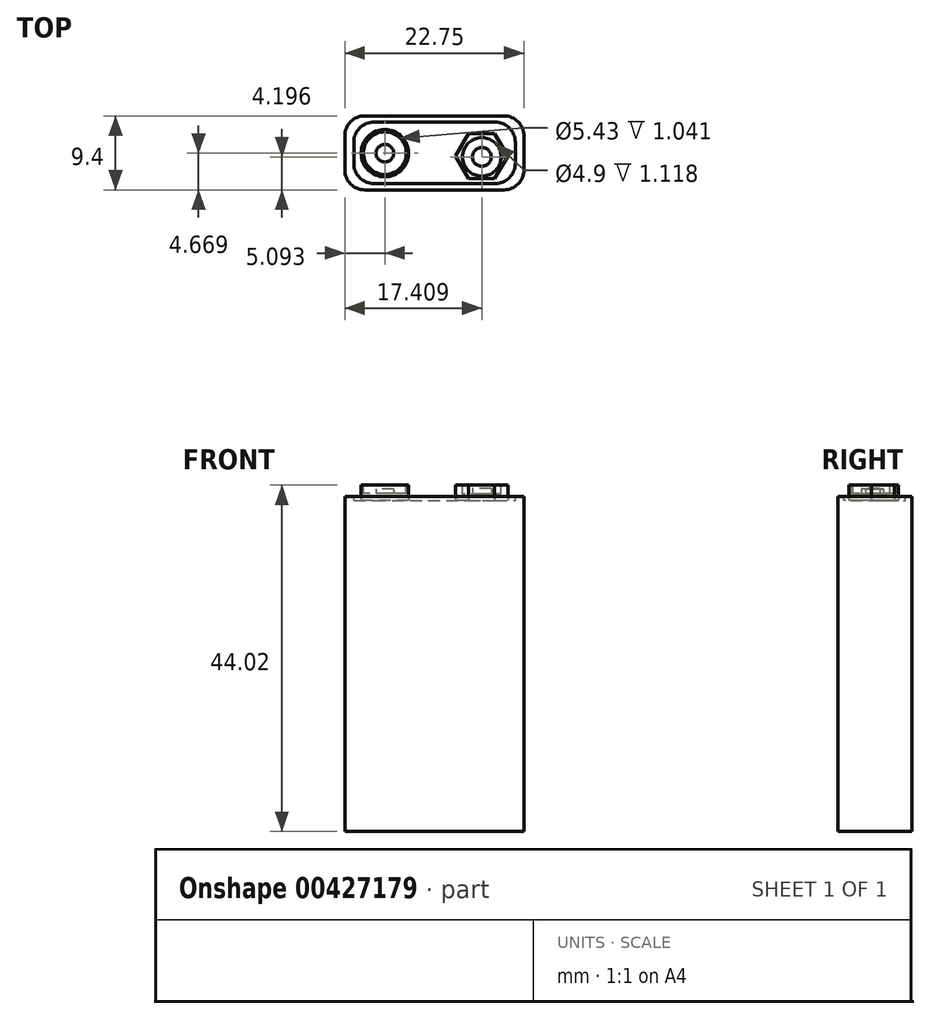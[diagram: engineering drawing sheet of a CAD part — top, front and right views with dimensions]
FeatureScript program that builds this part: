
annotation { "Feature Type Name" : "Feature", "Feature Type Description" : "" }
export const myFeature = defineFeature(function(context is Context, id is Id, definition is map)
    precondition{}
    {
        {
            var Q0;
            Q0=qCreatedBy(makeId("Front.planeOp"),FACE);
            var sketch = newSketch(context, id + "F0", { "sketchPlane" : qUnion([Q0])});
            skLineSegment(sketch, "E0.bottom", {"start": v(-9.62, 20.63) * mm, "end": v(13.13, 20.63) * mm});
            skLineSegment(sketch, "E0.top", {"start": v(-9.62, -21.92) * mm, "end": v(13.13, -21.92) * mm});
            skLineSegment(sketch, "E0.left", {"start": v(-9.62, 20.63) * mm, "end": v(-9.62, -21.92) * mm});
            skLineSegment(sketch, "E0.right", {"start": v(13.13, 20.63) * mm, "end": v(13.13, -21.92) * mm});
            skSolve(sketch);
        }
        {
            var Q0;
            Q0=makeQuery(id+"F0.imprint","IMPRINT",FACE,{"disambiguationData":[TD([[makeQuery(id+"F0.imprint","IMPRINT",EDGE,{"derivedFrom":sQuery(id+"F0.wireOp",EDGE,"E0.bottom")}),-1.0]])]});
            extrude(context, id + "F1", {"entities" : qUnion([Q0]), "depth" : 9.4 * mm});
        }
        {
            var Q0;
            Q0=makeQuery(id+"F1.opExtrude","CAP_EDGE",EDGE,{"disambiguationData":[OSD([sQuery(id+"F0.wireOp",EDGE,"E0.right")])],"isStart":false});
            var Q1;
            Q1=makeQuery(id+"F1.opExtrude","CAP_EDGE",EDGE,{"disambiguationData":[OSD([sQuery(id+"F0.wireOp",EDGE,"E0.left")])],"isStart":false});
            var Q2;
            Q2=makeQuery(id+"F1.opExtrude","CAP_EDGE",EDGE,{"disambiguationData":[OSD([sQuery(id+"F0.wireOp",EDGE,"E0.right")])],"isStart":true});
            var Q3;
            Q3=makeQuery(id+"F1.opExtrude","CAP_EDGE",EDGE,{"disambiguationData":[OSD([sQuery(id+"F0.wireOp",EDGE,"E0.left")])],"isStart":true});
            fillet(context, id + "F2", {"entities" : qUnion([Q0, Q1, Q2, Q3]), "radius" : 2.54 * mm, "tangentPropagation" : true, "allowEdgeOverflow" : false});
        }
        {
            var Q0;
            Q0=makeQuery(id+"F1.opExtrude","SWEPT_FACE",FACE,{"disambiguationData":[OSD([sQuery(id+"F0.wireOp",EDGE,"E0.bottom")])]});
            var sketch = newSketch(context, id + "F3", { "sketchPlane" : qUnion([Q0])});
            skLineSegment(sketch, "E1.bottom", {"start": v(-5.93, -0.8) * mm, "end": v(9.5, -0.8) * mm});
            skLineSegment(sketch, "E1.top", {"start": v(-5.93, -8.59) * mm, "end": v(9.5, -8.59) * mm});
            skLineSegment(sketch, "E1.left", {"start": v(-8.47, -3.34) * mm, "end": v(-8.47, -6.05) * mm});
            skLineSegment(sketch, "E1.right", {"start": v(12.03, -3.34) * mm, "end": v(12.03, -6.05) * mm});
            skPoint(sketch, "E2.visualSharp", {"position": v(12.03, -8.59) * mm});
            skArc(sketch, "E2.filletArc", {"start": v(9.5, -8.59) * mm, "mid": v(11.29, -7.85) * mm, "end": v(12.03, -6.05) * mm});
            skPoint(sketch, "E3.visualSharp", {"position": v(-8.47, -8.59) * mm});
            skArc(sketch, "E3.filletArc", {"start": v(-8.47, -6.05) * mm, "mid": v(-7.72, -7.85) * mm, "end": v(-5.93, -8.59) * mm});
            skPoint(sketch, "E4.visualSharp", {"position": v(-8.47, -0.8) * mm});
            skArc(sketch, "E4.filletArc", {"start": v(-5.93, -0.8) * mm, "mid": v(-7.72, -1.55) * mm, "end": v(-8.47, -3.34) * mm});
            skPoint(sketch, "E5.visualSharp", {"position": v(12.03, -0.8) * mm});
            skArc(sketch, "E5.filletArc", {"start": v(12.03, -3.34) * mm, "mid": v(11.29, -1.55) * mm, "end": v(9.5, -0.8) * mm});
            skSolve(sketch);
        }
        {
            var Q0;
            Q0=makeQuery(id+"F3.imprint","IMPRINT",FACE,{"disambiguationData":[TD([[makeQuery(id+"F3.imprint","IMPRINT",EDGE,{"derivedFrom":sQuery(id+"F3.wireOp",EDGE,"E1.bottom")}),-1.0]])]});
            extrude(context, id + "F4", {"entities" : qUnion([Q0]), "operationType" : NewBodyOperationType.REMOVE, "oppositeDirection" : true, "depth" : 0.5 * mm});
        }
        {
            var Q0;
            Q0=makeQuery(id+"F4.boolean.opBoolean","COPY",FACE,{"derivedFrom":makeQuery(id+"F4.opExtrude","CAP_FACE",FACE,{"disambiguationData":[OSD([sQuery(id+"F3.wireOp",EDGE,"E1.bottom"),sQuery(id+"F3.wireOp",EDGE,"E1.top"),sQuery(id+"F3.wireOp",EDGE,"E1.left"),sQuery(id+"F3.wireOp",EDGE,"E1.right"),sQuery(id+"F3.wireOp",EDGE,"E2.filletArc"),sQuery(id+"F3.wireOp",EDGE,"E3.filletArc"),sQuery(id+"F3.wireOp",EDGE,"E4.filletArc"),sQuery(id+"F3.wireOp",EDGE,"E5.filletArc")])],"isStart":false})});
            var sketch = newSketch(context, id + "F5", { "sketchPlane" : qUnion([Q0])});
            skCircle(sketch, "E6.cCircle", {"center": v(7.76, -5.1) * mm, "radius": 2.88 * mm, "construction": true});
            skLineSegment(sketch, "E6.0", {"start": v(6.1, -2.23) * mm, "end": v(9.42, -2.23) * mm});
            skLineSegment(sketch, "E6.1", {"start": v(9.42, -2.23) * mm, "end": v(11.08, -5.1) * mm});
            skLineSegment(sketch, "E6.2", {"start": v(11.08, -5.1) * mm, "end": v(9.42, -7.98) * mm});
            skLineSegment(sketch, "E6.3", {"start": v(9.42, -7.98) * mm, "end": v(6.1, -7.98) * mm});
            skLineSegment(sketch, "E6.4", {"start": v(6.1, -7.98) * mm, "end": v(4.44, -5.1) * mm});
            skLineSegment(sketch, "E6.5", {"start": v(4.44, -5.1) * mm, "end": v(6.1, -2.23) * mm});
            skPoint(sketch, "E6.0.midPoint", {"position": v(7.76, -2.23) * mm});
            skSolve(sketch);
        }
        {
            var Q0;
            Q0=makeQuery(id+"F5.imprint","IMPRINT",FACE,{"disambiguationData":[TD([[makeQuery(id+"F5.imprint","IMPRINT",EDGE,{"derivedFrom":sQuery(id+"F5.wireOp",EDGE,"E6.0")}),-1.0]])]});
            extrude(context, id + "F6", {"entities" : qUnion([Q0]), "operationType" : NewBodyOperationType.ADD, "depth" : 1.98 * mm});
        }
        {
            var Q0;
            Q0=makeQuery(id+"F4.boolean.opBoolean","COPY",FACE,{"derivedFrom":makeQuery(id+"F4.opExtrude","CAP_FACE",FACE,{"disambiguationData":[OSD([sQuery(id+"F3.wireOp",EDGE,"E1.bottom"),sQuery(id+"F3.wireOp",EDGE,"E1.top"),sQuery(id+"F3.wireOp",EDGE,"E1.left"),sQuery(id+"F3.wireOp",EDGE,"E1.right"),sQuery(id+"F3.wireOp",EDGE,"E2.filletArc"),sQuery(id+"F3.wireOp",EDGE,"E3.filletArc"),sQuery(id+"F3.wireOp",EDGE,"E4.filletArc"),sQuery(id+"F3.wireOp",EDGE,"E5.filletArc")])],"isStart":false})});
            var sketch = newSketch(context, id + "F7", { "sketchPlane" : qUnion([Q0])});
            skCircle(sketch, "E7", {"center": v(-4.53, -4.73) * mm, "radius": 3.01 * mm});
            skSolve(sketch);
        }
        {
            var Q0;
            Q0=makeQuery(id+"F7.imprint","IMPRINT",FACE,{"disambiguationData":[TD([[makeQuery(id+"F7.imprint","IMPRINT",EDGE,{"derivedFrom":sQuery(id+"F7.wireOp",EDGE,"E7")}),1.0]])]});
            extrude(context, id + "F8", {"entities" : qUnion([Q0]), "operationType" : NewBodyOperationType.ADD, "depth" : 1.98 * mm});
        }
        {
            var Q0;
            Q0=makeQuery(id+"F8.opExtrude","CAP_FACE",FACE,{"disambiguationData":[OSD([sQuery(id+"F7.wireOp",EDGE,"E7")])],"isStart":false});
            var sketch = newSketch(context, id + "F9", { "sketchPlane" : qUnion([Q0])});
            skCircle(sketch, "E8", {"center": v(-4.53, -4.73) * mm, "radius": 2.71 * mm});
            skSolve(sketch);
        }
        {
            var Q0;
            Q0=makeQuery(id+"F9.imprint","IMPRINT",FACE,{"disambiguationData":[TD([[makeQuery(id+"F9.imprint","IMPRINT",EDGE,{"derivedFrom":sQuery(id+"F9.wireOp",EDGE,"E8")}),1.0]])]});
            extrude(context, id + "F10", {"entities" : qUnion([Q0]), "operationType" : NewBodyOperationType.REMOVE, "oppositeDirection" : true, "depth" : 1.04 * mm});
        }
        {
            var Q0;
            Q0=makeQuery(id+"F10.boolean.opBoolean","COPY",FACE,{"derivedFrom":makeQuery(id+"F10.opExtrude","CAP_FACE",FACE,{"disambiguationData":[OSD([sQuery(id+"F9.wireOp",EDGE,"E8")])],"isStart":false})});
            var sketch = newSketch(context, id + "F11", { "sketchPlane" : qUnion([Q0])});
            skCircle(sketch, "E9", {"center": v(-4.53, -4.73) * mm, "radius": 1.12 * mm});
            skSolve(sketch);
        }
        {
            var Q0;
            Q0=makeQuery(id+"F11.imprint","IMPRINT",FACE,{"disambiguationData":[TD([[makeQuery(id+"F11.imprint","IMPRINT",EDGE,{"derivedFrom":sQuery(id+"F11.wireOp",EDGE,"E9")}),1.0]])]});
            extrude(context, id + "F12", {"entities" : qUnion([Q0]), "operationType" : NewBodyOperationType.ADD, "depth" : 0.56 * mm});
        }
        {
            var Q0;
            Q0=makeQuery(id+"F6.opExtrude","CAP_FACE",FACE,{"disambiguationData":[OSD([sQuery(id+"F5.wireOp",EDGE,"E6.0"),sQuery(id+"F5.wireOp",EDGE,"E6.1"),sQuery(id+"F5.wireOp",EDGE,"E6.2"),sQuery(id+"F5.wireOp",EDGE,"E6.3"),sQuery(id+"F5.wireOp",EDGE,"E6.4"),sQuery(id+"F5.wireOp",EDGE,"E6.5")])],"isStart":false});
            var sketch = newSketch(context, id + "F13", { "sketchPlane" : qUnion([Q0])});
            skCircle(sketch, "E10", {"center": v(7.79, -5.2) * mm, "radius": 2.45 * mm});
            skSolve(sketch);
        }
        {
            var Q0;
            Q0=makeQuery(id+"F13.imprint","IMPRINT",FACE,{"disambiguationData":[TD([[makeQuery(id+"F13.imprint","IMPRINT",EDGE,{"derivedFrom":sQuery(id+"F13.wireOp",EDGE,"E10")}),1.0]])]});
            extrude(context, id + "F14", {"entities" : qUnion([Q0]), "operationType" : NewBodyOperationType.REMOVE, "oppositeDirection" : true, "depth" : 1.12 * mm});
        }
        {
            var Q0;
            Q0=makeQuery(id+"F14.boolean.opBoolean","COPY",FACE,{"derivedFrom":makeQuery(id+"F14.opExtrude","CAP_FACE",FACE,{"disambiguationData":[OSD([sQuery(id+"F13.wireOp",EDGE,"E10")])],"isStart":false})});
            var sketch = newSketch(context, id + "F15", { "sketchPlane" : qUnion([Q0])});
            skCircle(sketch, "E11", {"center": v(7.79, -5.2) * mm, "radius": 1.2 * mm});
            skSolve(sketch);
        }
        {
            var Q0;
            Q0=makeQuery(id+"F15.imprint","IMPRINT",FACE,{"disambiguationData":[TD([[makeQuery(id+"F15.imprint","IMPRINT",EDGE,{"derivedFrom":sQuery(id+"F15.wireOp",EDGE,"E11")}),1.0]])]});
            extrude(context, id + "F16", {"entities" : qUnion([Q0]), "operationType" : NewBodyOperationType.ADD, "depth" : 0.66 * mm});
        }
    });
